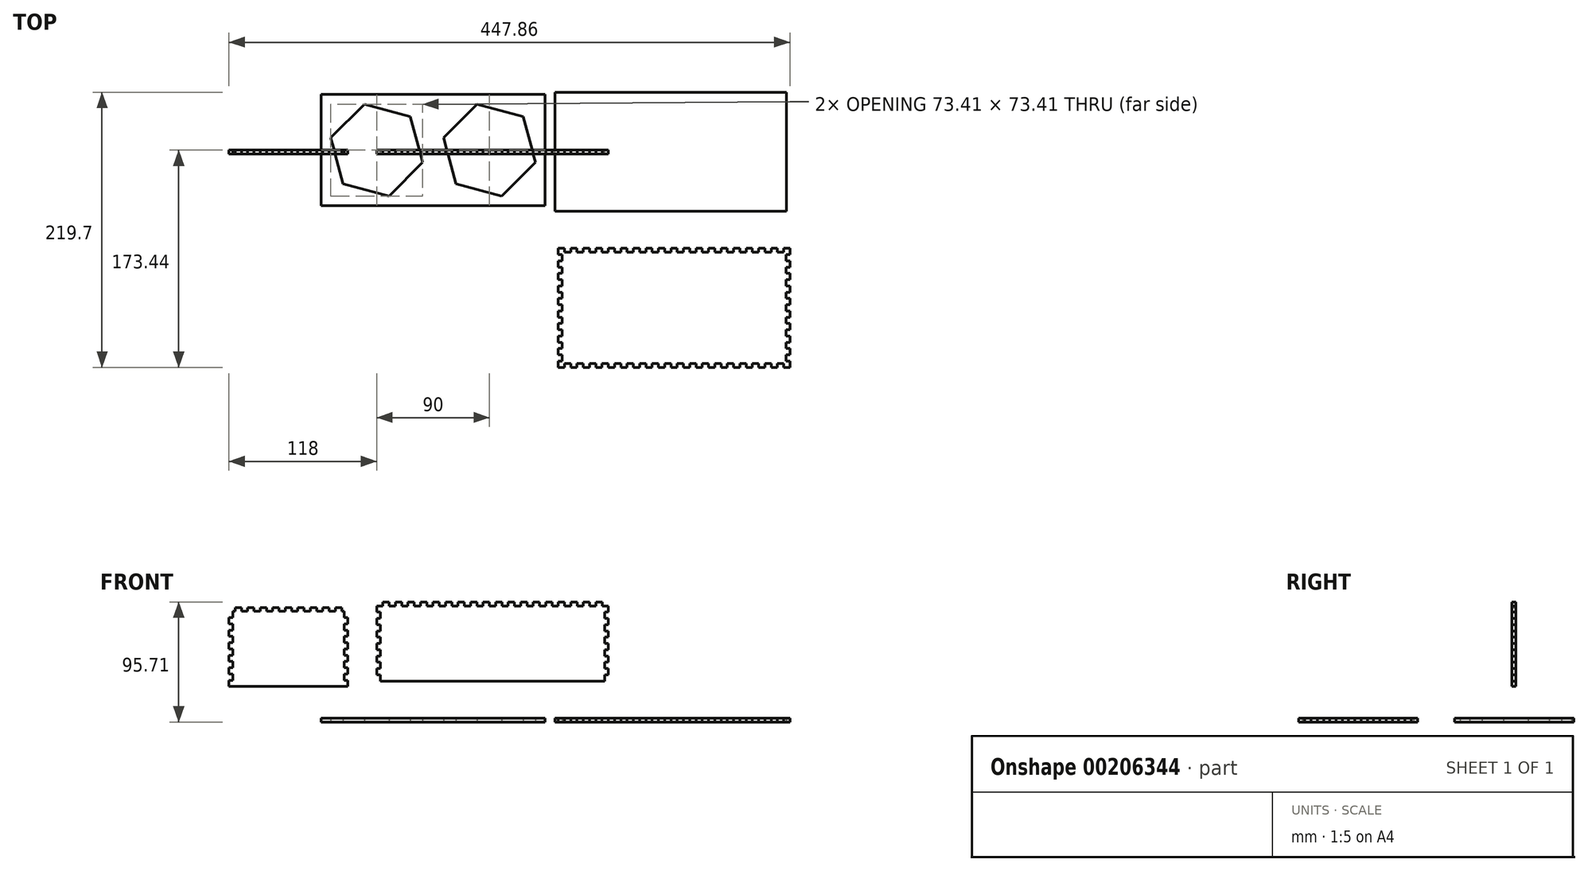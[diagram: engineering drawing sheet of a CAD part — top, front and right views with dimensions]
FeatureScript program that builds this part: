
annotation { "Feature Type Name" : "Feature", "Feature Type Description" : "" }
export const myFeature = defineFeature(function(context is Context, id is Id, definition is map)
    precondition{}
    {
        {
            var Q0;
            Q0=qCreatedBy(makeId("Top.planeOp"),FACE);
            var sketch = newSketch(context, id + "F0", { "sketchPlane" : qUnion([Q0])});
            skLineSegment(sketch, "E0.bottom", {"start": v(-89.5, 44.5) * mm, "end": v(89.5, 44.5) * mm});
            skLineSegment(sketch, "E0.top", {"start": v(-89.5, -44.5) * mm, "end": v(89.5, -44.5) * mm});
            skLineSegment(sketch, "E0.left", {"start": v(-89.5, 44.5) * mm, "end": v(-89.5, -44.5) * mm});
            skLineSegment(sketch, "E0.right", {"start": v(89.5, 44.5) * mm, "end": v(89.5, -44.5) * mm});
            skCircle(sketch, "E1.cCircle", {"center": v(-45, 0) * mm, "radius": 32.9 * mm, "construction": true});
            skLineSegment(sketch, "E1.0", {"start": v(-8.3, -9.84) * mm, "end": v(-35.16, -36.7) * mm});
            skLineSegment(sketch, "E1.1", {"start": v(-35.16, -36.7) * mm, "end": v(-71.87, -26.87) * mm});
            skLineSegment(sketch, "E1.2", {"start": v(-71.87, -26.87) * mm, "end": v(-81.7, 9.84) * mm});
            skLineSegment(sketch, "E1.3", {"start": v(-81.7, 9.84) * mm, "end": v(-54.84, 36.7) * mm});
            skLineSegment(sketch, "E1.4", {"start": v(-54.84, 36.7) * mm, "end": v(-18.13, 26.87) * mm});
            skLineSegment(sketch, "E1.5", {"start": v(-18.13, 26.87) * mm, "end": v(-8.3, -9.84) * mm});
            skPoint(sketch, "E1.0.midPoint", {"position": v(-21.73, -23.27) * mm});
            skCircle(sketch, "E2.cCircle", {"center": v(45, 0) * mm, "radius": 32.9 * mm, "construction": true});
            skLineSegment(sketch, "E2.0", {"start": v(81.7, -9.84) * mm, "end": v(54.84, -36.7) * mm});
            skLineSegment(sketch, "E2.1", {"start": v(54.84, -36.7) * mm, "end": v(18.13, -26.87) * mm});
            skLineSegment(sketch, "E2.2", {"start": v(18.13, -26.87) * mm, "end": v(8.3, 9.84) * mm});
            skLineSegment(sketch, "E2.3", {"start": v(8.3, 9.84) * mm, "end": v(35.16, 36.7) * mm});
            skLineSegment(sketch, "E2.4", {"start": v(35.16, 36.7) * mm, "end": v(71.87, 26.87) * mm});
            skLineSegment(sketch, "E2.5", {"start": v(71.87, 26.87) * mm, "end": v(81.7, -9.84) * mm});
            skPoint(sketch, "E2.0.midPoint", {"position": v(68.27, -23.27) * mm});
            skLineSegment(sketch, "E3", {"start": v(-45, 0) * mm, "end": v(45, 0) * mm, "construction": true});
            skSolve(sketch);
        }
        {
            var Q0;
            Q0 = qSketchRegion(id + "F0", true);
            extrude(context, id + "F1", {"entities" : qUnion([Q0]), "depth" : 3 * mm});
        }
        {
            var Q0;
            Q0=qCreatedBy(makeId("Top.planeOp"),FACE);
            var sketch = newSketch(context, id + "F2", { "sketchPlane" : qUnion([Q0])});
            skLineSegment(sketch, "E4.bottom", {"start": v(97.21, -48.74) * mm, "end": v(282.21, -48.74) * mm});
            skLineSegment(sketch, "E4.top", {"start": v(97.21, 46.26) * mm, "end": v(282.21, 46.26) * mm});
            skLineSegment(sketch, "E4.left", {"start": v(97.21, -48.74) * mm, "end": v(97.21, 46.26) * mm});
            skLineSegment(sketch, "E4.right", {"start": v(282.21, -48.74) * mm, "end": v(282.21, 46.26) * mm});
            skSolve(sketch);
        }
        {
            var Q0;
            Q0 = qSketchRegion(id + "F2", true);
            extrude(context, id + "F3", {"entities" : qUnion([Q0]), "depth" : 3 * mm});
        }
        {
            var Q0;
            Q0=qCreatedBy(makeId("Top.planeOp"),FACE);
            var sketch = newSketch(context, id + "F4", { "sketchPlane" : qUnion([Q0])});
            skLineSegment(sketch, "E5", {"start": v(99.86, -173.44) * mm, "end": v(104.86, -173.44) * mm});
            skLineSegment(sketch, "E6", {"start": v(104.86, -173.44) * mm, "end": v(104.86, -170.44) * mm});
            skLineSegment(sketch, "E7", {"start": v(104.86, -170.44) * mm, "end": v(109.86, -170.44) * mm});
            skLineSegment(sketch, "E8", {"start": v(109.86, -170.44) * mm, "end": v(109.86, -173.44) * mm});
            skLineSegment(sketch, "E9.1.0.0", {"start": v(114.86, -170.44) * mm, "end": v(119.86, -170.44) * mm});
            skLineSegment(sketch, "E9.1.0.1", {"start": v(119.86, -170.44) * mm, "end": v(119.86, -173.44) * mm});
            skLineSegment(sketch, "E9.1.0.2", {"start": v(114.86, -173.44) * mm, "end": v(114.86, -170.44) * mm});
            skLineSegment(sketch, "E9.1.0.3", {"start": v(109.86, -173.44) * mm, "end": v(114.86, -173.44) * mm});
            skLineSegment(sketch, "E9.2.0.0", {"start": v(124.86, -170.44) * mm, "end": v(129.86, -170.44) * mm});
            skLineSegment(sketch, "E9.2.0.1", {"start": v(129.86, -170.44) * mm, "end": v(129.86, -173.44) * mm});
            skLineSegment(sketch, "E9.2.0.2", {"start": v(124.86, -173.44) * mm, "end": v(124.86, -170.44) * mm});
            skLineSegment(sketch, "E9.2.0.3", {"start": v(119.86, -173.44) * mm, "end": v(124.86, -173.44) * mm});
            skLineSegment(sketch, "E9.3.0.0", {"start": v(134.86, -170.44) * mm, "end": v(139.86, -170.44) * mm});
            skLineSegment(sketch, "E9.3.0.1", {"start": v(139.86, -170.44) * mm, "end": v(139.86, -173.44) * mm});
            skLineSegment(sketch, "E9.3.0.2", {"start": v(134.86, -173.44) * mm, "end": v(134.86, -170.44) * mm});
            skLineSegment(sketch, "E9.3.0.3", {"start": v(129.86, -173.44) * mm, "end": v(134.86, -173.44) * mm});
            skLineSegment(sketch, "E9.4.0.0", {"start": v(144.86, -170.44) * mm, "end": v(149.86, -170.44) * mm});
            skLineSegment(sketch, "E9.4.0.1", {"start": v(149.86, -170.44) * mm, "end": v(149.86, -173.44) * mm});
            skLineSegment(sketch, "E9.4.0.2", {"start": v(144.86, -173.44) * mm, "end": v(144.86, -170.44) * mm});
            skLineSegment(sketch, "E9.4.0.3", {"start": v(139.86, -173.44) * mm, "end": v(144.86, -173.44) * mm});
            skLineSegment(sketch, "E9.5.0.0", {"start": v(154.86, -170.44) * mm, "end": v(159.86, -170.44) * mm});
            skLineSegment(sketch, "E9.5.0.1", {"start": v(159.86, -170.44) * mm, "end": v(159.86, -173.44) * mm});
            skLineSegment(sketch, "E9.5.0.2", {"start": v(154.86, -173.44) * mm, "end": v(154.86, -170.44) * mm});
            skLineSegment(sketch, "E9.5.0.3", {"start": v(149.86, -173.44) * mm, "end": v(154.86, -173.44) * mm});
            skLineSegment(sketch, "E9.6.0.0", {"start": v(164.86, -170.44) * mm, "end": v(169.86, -170.44) * mm});
            skLineSegment(sketch, "E9.6.0.1", {"start": v(169.86, -170.44) * mm, "end": v(169.86, -173.44) * mm});
            skLineSegment(sketch, "E9.6.0.2", {"start": v(164.86, -173.44) * mm, "end": v(164.86, -170.44) * mm});
            skLineSegment(sketch, "E9.6.0.3", {"start": v(159.86, -173.44) * mm, "end": v(164.86, -173.44) * mm});
            skLineSegment(sketch, "E9.7.0.0", {"start": v(174.86, -170.44) * mm, "end": v(179.86, -170.44) * mm});
            skLineSegment(sketch, "E9.7.0.1", {"start": v(179.86, -170.44) * mm, "end": v(179.86, -173.44) * mm});
            skLineSegment(sketch, "E9.7.0.2", {"start": v(174.86, -173.44) * mm, "end": v(174.86, -170.44) * mm});
            skLineSegment(sketch, "E9.7.0.3", {"start": v(169.86, -173.44) * mm, "end": v(174.86, -173.44) * mm});
            skLineSegment(sketch, "E9.8.0.0", {"start": v(184.86, -170.44) * mm, "end": v(189.86, -170.44) * mm});
            skLineSegment(sketch, "E9.8.0.1", {"start": v(189.86, -170.44) * mm, "end": v(189.86, -173.44) * mm});
            skLineSegment(sketch, "E9.8.0.2", {"start": v(184.86, -173.44) * mm, "end": v(184.86, -170.44) * mm});
            skLineSegment(sketch, "E9.8.0.3", {"start": v(179.86, -173.44) * mm, "end": v(184.86, -173.44) * mm});
            skLineSegment(sketch, "E9.9.0.0", {"start": v(194.86, -170.44) * mm, "end": v(199.86, -170.44) * mm});
            skLineSegment(sketch, "E9.9.0.1", {"start": v(199.86, -170.44) * mm, "end": v(199.86, -173.44) * mm});
            skLineSegment(sketch, "E9.9.0.2", {"start": v(194.86, -173.44) * mm, "end": v(194.86, -170.44) * mm});
            skLineSegment(sketch, "E9.9.0.3", {"start": v(189.86, -173.44) * mm, "end": v(194.86, -173.44) * mm});
            skLineSegment(sketch, "E9.10.0.0", {"start": v(204.86, -170.44) * mm, "end": v(209.86, -170.44) * mm});
            skLineSegment(sketch, "E9.10.0.1", {"start": v(209.86, -170.44) * mm, "end": v(209.86, -173.44) * mm});
            skLineSegment(sketch, "E9.10.0.2", {"start": v(204.86, -173.44) * mm, "end": v(204.86, -170.44) * mm});
            skLineSegment(sketch, "E9.10.0.3", {"start": v(199.86, -173.44) * mm, "end": v(204.86, -173.44) * mm});
            skLineSegment(sketch, "E9.11.0.0", {"start": v(214.86, -170.44) * mm, "end": v(219.86, -170.44) * mm});
            skLineSegment(sketch, "E9.11.0.1", {"start": v(219.86, -170.44) * mm, "end": v(219.86, -173.44) * mm});
            skLineSegment(sketch, "E9.11.0.2", {"start": v(214.86, -173.44) * mm, "end": v(214.86, -170.44) * mm});
            skLineSegment(sketch, "E9.11.0.3", {"start": v(209.86, -173.44) * mm, "end": v(214.86, -173.44) * mm});
            skLineSegment(sketch, "E9.12.0.0", {"start": v(224.86, -170.44) * mm, "end": v(229.86, -170.44) * mm});
            skLineSegment(sketch, "E9.12.0.1", {"start": v(229.86, -170.44) * mm, "end": v(229.86, -173.44) * mm});
            skLineSegment(sketch, "E9.12.0.2", {"start": v(224.86, -173.44) * mm, "end": v(224.86, -170.44) * mm});
            skLineSegment(sketch, "E9.12.0.3", {"start": v(219.86, -173.44) * mm, "end": v(224.86, -173.44) * mm});
            skLineSegment(sketch, "E9.13.0.0", {"start": v(234.86, -170.44) * mm, "end": v(239.86, -170.44) * mm});
            skLineSegment(sketch, "E9.13.0.1", {"start": v(239.86, -170.44) * mm, "end": v(239.86, -173.44) * mm});
            skLineSegment(sketch, "E9.13.0.2", {"start": v(234.86, -173.44) * mm, "end": v(234.86, -170.44) * mm});
            skLineSegment(sketch, "E9.13.0.3", {"start": v(229.86, -173.44) * mm, "end": v(234.86, -173.44) * mm});
            skLineSegment(sketch, "E9.14.0.0", {"start": v(244.86, -170.44) * mm, "end": v(249.86, -170.44) * mm});
            skLineSegment(sketch, "E9.14.0.1", {"start": v(249.86, -170.44) * mm, "end": v(249.86, -173.44) * mm});
            skLineSegment(sketch, "E9.14.0.2", {"start": v(244.86, -173.44) * mm, "end": v(244.86, -170.44) * mm});
            skLineSegment(sketch, "E9.14.0.3", {"start": v(239.86, -173.44) * mm, "end": v(244.86, -173.44) * mm});
            skLineSegment(sketch, "E9.15.0.0", {"start": v(254.86, -170.44) * mm, "end": v(259.86, -170.44) * mm});
            skLineSegment(sketch, "E9.15.0.1", {"start": v(259.86, -170.44) * mm, "end": v(259.86, -173.44) * mm});
            skLineSegment(sketch, "E9.15.0.2", {"start": v(254.86, -173.44) * mm, "end": v(254.86, -170.44) * mm});
            skLineSegment(sketch, "E9.15.0.3", {"start": v(249.86, -173.44) * mm, "end": v(254.86, -173.44) * mm});
            skLineSegment(sketch, "E9.16.0.0", {"start": v(264.86, -170.44) * mm, "end": v(269.86, -170.44) * mm});
            skLineSegment(sketch, "E9.16.0.1", {"start": v(269.86, -170.44) * mm, "end": v(269.86, -173.44) * mm});
            skLineSegment(sketch, "E9.16.0.2", {"start": v(264.86, -173.44) * mm, "end": v(264.86, -170.44) * mm});
            skLineSegment(sketch, "E9.16.0.3", {"start": v(259.86, -173.44) * mm, "end": v(264.86, -173.44) * mm});
            skLineSegment(sketch, "E9.17.0.0", {"start": v(274.86, -170.44) * mm, "end": v(279.86, -170.44) * mm});
            skLineSegment(sketch, "E9.17.0.1", {"start": v(279.86, -170.44) * mm, "end": v(279.86, -173.44) * mm});
            skLineSegment(sketch, "E9.17.0.2", {"start": v(274.86, -173.44) * mm, "end": v(274.86, -170.44) * mm});
            skLineSegment(sketch, "E9.17.0.3", {"start": v(269.86, -173.44) * mm, "end": v(274.86, -173.44) * mm});
            skLineSegment(sketch, "E9.direction1", {"start": v(99.86, -173.44) * mm, "end": v(109.86, -173.44) * mm, "construction": true});
            skLineSegment(sketch, "E10", {"start": v(279.86, -173.44) * mm, "end": v(284.86, -173.44) * mm});
            skLineSegment(sketch, "E11", {"start": v(99.86, -78.44) * mm, "end": v(104.86, -78.44) * mm});
            skLineSegment(sketch, "E12", {"start": v(104.86, -78.44) * mm, "end": v(104.86, -81.44) * mm});
            skLineSegment(sketch, "E13", {"start": v(104.86, -81.44) * mm, "end": v(109.86, -81.44) * mm});
            skLineSegment(sketch, "E14", {"start": v(109.86, -81.44) * mm, "end": v(109.86, -78.44) * mm});
            skLineSegment(sketch, "E15.1.0.0", {"start": v(109.86, -78.44) * mm, "end": v(114.86, -78.44) * mm});
            skLineSegment(sketch, "E15.1.0.1", {"start": v(114.86, -78.44) * mm, "end": v(114.86, -81.44) * mm});
            skLineSegment(sketch, "E15.1.0.2", {"start": v(119.86, -81.44) * mm, "end": v(119.86, -78.44) * mm});
            skLineSegment(sketch, "E15.1.0.3", {"start": v(114.86, -81.44) * mm, "end": v(119.86, -81.44) * mm});
            skLineSegment(sketch, "E15.2.0.0", {"start": v(119.86, -78.44) * mm, "end": v(124.86, -78.44) * mm});
            skLineSegment(sketch, "E15.2.0.1", {"start": v(124.86, -78.44) * mm, "end": v(124.86, -81.44) * mm});
            skLineSegment(sketch, "E15.2.0.2", {"start": v(129.86, -81.44) * mm, "end": v(129.86, -78.44) * mm});
            skLineSegment(sketch, "E15.2.0.3", {"start": v(124.86, -81.44) * mm, "end": v(129.86, -81.44) * mm});
            skLineSegment(sketch, "E15.3.0.0", {"start": v(129.86, -78.44) * mm, "end": v(134.86, -78.44) * mm});
            skLineSegment(sketch, "E15.3.0.1", {"start": v(134.86, -78.44) * mm, "end": v(134.86, -81.44) * mm});
            skLineSegment(sketch, "E15.3.0.2", {"start": v(139.86, -81.44) * mm, "end": v(139.86, -78.44) * mm});
            skLineSegment(sketch, "E15.3.0.3", {"start": v(134.86, -81.44) * mm, "end": v(139.86, -81.44) * mm});
            skLineSegment(sketch, "E15.4.0.0", {"start": v(139.86, -78.44) * mm, "end": v(144.86, -78.44) * mm});
            skLineSegment(sketch, "E15.4.0.1", {"start": v(144.86, -78.44) * mm, "end": v(144.86, -81.44) * mm});
            skLineSegment(sketch, "E15.4.0.2", {"start": v(149.86, -81.44) * mm, "end": v(149.86, -78.44) * mm});
            skLineSegment(sketch, "E15.4.0.3", {"start": v(144.86, -81.44) * mm, "end": v(149.86, -81.44) * mm});
            skLineSegment(sketch, "E15.5.0.0", {"start": v(149.86, -78.44) * mm, "end": v(154.86, -78.44) * mm});
            skLineSegment(sketch, "E15.5.0.1", {"start": v(154.86, -78.44) * mm, "end": v(154.86, -81.44) * mm});
            skLineSegment(sketch, "E15.5.0.2", {"start": v(159.86, -81.44) * mm, "end": v(159.86, -78.44) * mm});
            skLineSegment(sketch, "E15.5.0.3", {"start": v(154.86, -81.44) * mm, "end": v(159.86, -81.44) * mm});
            skLineSegment(sketch, "E15.6.0.0", {"start": v(159.86, -78.44) * mm, "end": v(164.86, -78.44) * mm});
            skLineSegment(sketch, "E15.6.0.1", {"start": v(164.86, -78.44) * mm, "end": v(164.86, -81.44) * mm});
            skLineSegment(sketch, "E15.6.0.2", {"start": v(169.86, -81.44) * mm, "end": v(169.86, -78.44) * mm});
            skLineSegment(sketch, "E15.6.0.3", {"start": v(164.86, -81.44) * mm, "end": v(169.86, -81.44) * mm});
            skLineSegment(sketch, "E15.7.0.0", {"start": v(169.86, -78.44) * mm, "end": v(174.86, -78.44) * mm});
            skLineSegment(sketch, "E15.7.0.1", {"start": v(174.86, -78.44) * mm, "end": v(174.86, -81.44) * mm});
            skLineSegment(sketch, "E15.7.0.2", {"start": v(179.86, -81.44) * mm, "end": v(179.86, -78.44) * mm});
            skLineSegment(sketch, "E15.7.0.3", {"start": v(174.86, -81.44) * mm, "end": v(179.86, -81.44) * mm});
            skLineSegment(sketch, "E15.8.0.0", {"start": v(179.86, -78.44) * mm, "end": v(184.86, -78.44) * mm});
            skLineSegment(sketch, "E15.8.0.1", {"start": v(184.86, -78.44) * mm, "end": v(184.86, -81.44) * mm});
            skLineSegment(sketch, "E15.8.0.2", {"start": v(189.86, -81.44) * mm, "end": v(189.86, -78.44) * mm});
            skLineSegment(sketch, "E15.8.0.3", {"start": v(184.86, -81.44) * mm, "end": v(189.86, -81.44) * mm});
            skLineSegment(sketch, "E15.9.0.0", {"start": v(189.86, -78.44) * mm, "end": v(194.86, -78.44) * mm});
            skLineSegment(sketch, "E15.9.0.1", {"start": v(194.86, -78.44) * mm, "end": v(194.86, -81.44) * mm});
            skLineSegment(sketch, "E15.9.0.2", {"start": v(199.86, -81.44) * mm, "end": v(199.86, -78.44) * mm});
            skLineSegment(sketch, "E15.9.0.3", {"start": v(194.86, -81.44) * mm, "end": v(199.86, -81.44) * mm});
            skLineSegment(sketch, "E15.10.0.0", {"start": v(199.86, -78.44) * mm, "end": v(204.86, -78.44) * mm});
            skLineSegment(sketch, "E15.10.0.1", {"start": v(204.86, -78.44) * mm, "end": v(204.86, -81.44) * mm});
            skLineSegment(sketch, "E15.10.0.2", {"start": v(209.86, -81.44) * mm, "end": v(209.86, -78.44) * mm});
            skLineSegment(sketch, "E15.10.0.3", {"start": v(204.86, -81.44) * mm, "end": v(209.86, -81.44) * mm});
            skLineSegment(sketch, "E15.11.0.0", {"start": v(209.86, -78.44) * mm, "end": v(214.86, -78.44) * mm});
            skLineSegment(sketch, "E15.11.0.1", {"start": v(214.86, -78.44) * mm, "end": v(214.86, -81.44) * mm});
            skLineSegment(sketch, "E15.11.0.2", {"start": v(219.86, -81.44) * mm, "end": v(219.86, -78.44) * mm});
            skLineSegment(sketch, "E15.11.0.3", {"start": v(214.86, -81.44) * mm, "end": v(219.86, -81.44) * mm});
            skLineSegment(sketch, "E15.12.0.0", {"start": v(219.86, -78.44) * mm, "end": v(224.86, -78.44) * mm});
            skLineSegment(sketch, "E15.12.0.1", {"start": v(224.86, -78.44) * mm, "end": v(224.86, -81.44) * mm});
            skLineSegment(sketch, "E15.12.0.2", {"start": v(229.86, -81.44) * mm, "end": v(229.86, -78.44) * mm});
            skLineSegment(sketch, "E15.12.0.3", {"start": v(224.86, -81.44) * mm, "end": v(229.86, -81.44) * mm});
            skLineSegment(sketch, "E15.13.0.0", {"start": v(229.86, -78.44) * mm, "end": v(234.86, -78.44) * mm});
            skLineSegment(sketch, "E15.13.0.1", {"start": v(234.86, -78.44) * mm, "end": v(234.86, -81.44) * mm});
            skLineSegment(sketch, "E15.13.0.2", {"start": v(239.86, -81.44) * mm, "end": v(239.86, -78.44) * mm});
            skLineSegment(sketch, "E15.13.0.3", {"start": v(234.86, -81.44) * mm, "end": v(239.86, -81.44) * mm});
            skLineSegment(sketch, "E15.14.0.0", {"start": v(239.86, -78.44) * mm, "end": v(244.86, -78.44) * mm});
            skLineSegment(sketch, "E15.14.0.1", {"start": v(244.86, -78.44) * mm, "end": v(244.86, -81.44) * mm});
            skLineSegment(sketch, "E15.14.0.2", {"start": v(249.86, -81.44) * mm, "end": v(249.86, -78.44) * mm});
            skLineSegment(sketch, "E15.14.0.3", {"start": v(244.86, -81.44) * mm, "end": v(249.86, -81.44) * mm});
            skLineSegment(sketch, "E15.15.0.0", {"start": v(249.86, -78.44) * mm, "end": v(254.86, -78.44) * mm});
            skLineSegment(sketch, "E15.15.0.1", {"start": v(254.86, -78.44) * mm, "end": v(254.86, -81.44) * mm});
            skLineSegment(sketch, "E15.15.0.2", {"start": v(259.86, -81.44) * mm, "end": v(259.86, -78.44) * mm});
            skLineSegment(sketch, "E15.15.0.3", {"start": v(254.86, -81.44) * mm, "end": v(259.86, -81.44) * mm});
            skLineSegment(sketch, "E15.16.0.0", {"start": v(259.86, -78.44) * mm, "end": v(264.86, -78.44) * mm});
            skLineSegment(sketch, "E15.16.0.1", {"start": v(264.86, -78.44) * mm, "end": v(264.86, -81.44) * mm});
            skLineSegment(sketch, "E15.16.0.2", {"start": v(269.86, -81.44) * mm, "end": v(269.86, -78.44) * mm});
            skLineSegment(sketch, "E15.16.0.3", {"start": v(264.86, -81.44) * mm, "end": v(269.86, -81.44) * mm});
            skLineSegment(sketch, "E15.17.0.0", {"start": v(269.86, -78.44) * mm, "end": v(274.86, -78.44) * mm});
            skLineSegment(sketch, "E15.17.0.1", {"start": v(274.86, -78.44) * mm, "end": v(274.86, -81.44) * mm});
            skLineSegment(sketch, "E15.17.0.2", {"start": v(279.86, -81.44) * mm, "end": v(279.86, -78.44) * mm});
            skLineSegment(sketch, "E15.17.0.3", {"start": v(274.86, -81.44) * mm, "end": v(279.86, -81.44) * mm});
            skLineSegment(sketch, "E15.direction1", {"start": v(99.86, -78.44) * mm, "end": v(109.86, -78.44) * mm, "construction": true});
            skLineSegment(sketch, "E16", {"start": v(279.86, -78.44) * mm, "end": v(284.86, -78.44) * mm});
            skLineSegment(sketch, "E17", {"start": v(99.86, -78.44) * mm, "end": v(99.86, -83.44) * mm});
            skLineSegment(sketch, "E18", {"start": v(99.86, -83.44) * mm, "end": v(102.86, -83.44) * mm});
            skLineSegment(sketch, "E19", {"start": v(102.86, -83.44) * mm, "end": v(102.86, -88.44) * mm});
            skLineSegment(sketch, "E20", {"start": v(102.86, -88.44) * mm, "end": v(99.86, -88.44) * mm});
            skLineSegment(sketch, "E21.0.1.0", {"start": v(99.86, -88.44) * mm, "end": v(99.86, -93.44) * mm});
            skLineSegment(sketch, "E21.0.1.1", {"start": v(102.86, -98.44) * mm, "end": v(99.86, -98.44) * mm});
            skLineSegment(sketch, "E21.0.1.2", {"start": v(102.86, -93.44) * mm, "end": v(102.86, -98.44) * mm});
            skLineSegment(sketch, "E21.0.1.3", {"start": v(99.86, -93.44) * mm, "end": v(102.86, -93.44) * mm});
            skLineSegment(sketch, "E21.0.2.0", {"start": v(99.86, -98.44) * mm, "end": v(99.86, -103.44) * mm});
            skLineSegment(sketch, "E21.0.2.1", {"start": v(102.86, -108.44) * mm, "end": v(99.86, -108.44) * mm});
            skLineSegment(sketch, "E21.0.2.2", {"start": v(102.86, -103.44) * mm, "end": v(102.86, -108.44) * mm});
            skLineSegment(sketch, "E21.0.2.3", {"start": v(99.86, -103.44) * mm, "end": v(102.86, -103.44) * mm});
            skLineSegment(sketch, "E21.0.3.0", {"start": v(99.86, -108.44) * mm, "end": v(99.86, -113.44) * mm});
            skLineSegment(sketch, "E21.0.3.1", {"start": v(102.86, -118.44) * mm, "end": v(99.86, -118.44) * mm});
            skLineSegment(sketch, "E21.0.3.2", {"start": v(102.86, -113.44) * mm, "end": v(102.86, -118.44) * mm});
            skLineSegment(sketch, "E21.0.3.3", {"start": v(99.86, -113.44) * mm, "end": v(102.86, -113.44) * mm});
            skLineSegment(sketch, "E21.0.4.0", {"start": v(99.86, -118.44) * mm, "end": v(99.86, -123.44) * mm});
            skLineSegment(sketch, "E21.0.4.1", {"start": v(102.86, -128.44) * mm, "end": v(99.86, -128.44) * mm});
            skLineSegment(sketch, "E21.0.4.2", {"start": v(102.86, -123.44) * mm, "end": v(102.86, -128.44) * mm});
            skLineSegment(sketch, "E21.0.4.3", {"start": v(99.86, -123.44) * mm, "end": v(102.86, -123.44) * mm});
            skLineSegment(sketch, "E21.0.5.0", {"start": v(99.86, -128.44) * mm, "end": v(99.86, -133.44) * mm});
            skLineSegment(sketch, "E21.0.5.1", {"start": v(102.86, -138.44) * mm, "end": v(99.86, -138.44) * mm});
            skLineSegment(sketch, "E21.0.5.2", {"start": v(102.86, -133.44) * mm, "end": v(102.86, -138.44) * mm});
            skLineSegment(sketch, "E21.0.5.3", {"start": v(99.86, -133.44) * mm, "end": v(102.86, -133.44) * mm});
            skLineSegment(sketch, "E21.0.6.0", {"start": v(99.86, -138.44) * mm, "end": v(99.86, -143.44) * mm});
            skLineSegment(sketch, "E21.0.6.1", {"start": v(102.86, -148.44) * mm, "end": v(99.86, -148.44) * mm});
            skLineSegment(sketch, "E21.0.6.2", {"start": v(102.86, -143.44) * mm, "end": v(102.86, -148.44) * mm});
            skLineSegment(sketch, "E21.0.6.3", {"start": v(99.86, -143.44) * mm, "end": v(102.86, -143.44) * mm});
            skLineSegment(sketch, "E21.0.7.0", {"start": v(99.86, -148.44) * mm, "end": v(99.86, -153.44) * mm});
            skLineSegment(sketch, "E21.0.7.1", {"start": v(102.86, -158.44) * mm, "end": v(99.86, -158.44) * mm});
            skLineSegment(sketch, "E21.0.7.2", {"start": v(102.86, -153.44) * mm, "end": v(102.86, -158.44) * mm});
            skLineSegment(sketch, "E21.0.7.3", {"start": v(99.86, -153.44) * mm, "end": v(102.86, -153.44) * mm});
            skLineSegment(sketch, "E21.0.8.0", {"start": v(99.86, -158.44) * mm, "end": v(99.86, -163.44) * mm});
            skLineSegment(sketch, "E21.0.8.1", {"start": v(102.86, -168.44) * mm, "end": v(99.86, -168.44) * mm});
            skLineSegment(sketch, "E21.0.8.2", {"start": v(102.86, -163.44) * mm, "end": v(102.86, -168.44) * mm});
            skLineSegment(sketch, "E21.0.8.3", {"start": v(99.86, -163.44) * mm, "end": v(102.86, -163.44) * mm});
            skLineSegment(sketch, "E21.direction1", {"start": v(99.86, -88.44) * mm, "end": v(124.86, -88.44) * mm, "construction": true});
            skLineSegment(sketch, "E21.direction2", {"start": v(99.86, -88.44) * mm, "end": v(99.86, -98.44) * mm, "construction": true});
            skLineSegment(sketch, "E22", {"start": v(99.86, -168.44) * mm, "end": v(99.86, -173.44) * mm});
            skLineSegment(sketch, "E23", {"start": v(284.86, -78.44) * mm, "end": v(284.86, -83.44) * mm});
            skLineSegment(sketch, "E24", {"start": v(284.86, -83.44) * mm, "end": v(281.86, -83.44) * mm});
            skLineSegment(sketch, "E25", {"start": v(281.86, -83.44) * mm, "end": v(281.86, -88.44) * mm});
            skLineSegment(sketch, "E26", {"start": v(281.86, -88.44) * mm, "end": v(284.86, -88.44) * mm});
            skLineSegment(sketch, "E27.0.1.0", {"start": v(281.86, -93.44) * mm, "end": v(281.86, -98.44) * mm});
            skLineSegment(sketch, "E27.0.1.1", {"start": v(284.86, -88.44) * mm, "end": v(284.86, -93.44) * mm});
            skLineSegment(sketch, "E27.0.1.2", {"start": v(284.86, -93.44) * mm, "end": v(281.86, -93.44) * mm});
            skLineSegment(sketch, "E27.0.1.3", {"start": v(281.86, -98.44) * mm, "end": v(284.86, -98.44) * mm});
            skLineSegment(sketch, "E27.0.2.0", {"start": v(281.86, -103.44) * mm, "end": v(281.86, -108.44) * mm});
            skLineSegment(sketch, "E27.0.2.1", {"start": v(284.86, -98.44) * mm, "end": v(284.86, -103.44) * mm});
            skLineSegment(sketch, "E27.0.2.2", {"start": v(284.86, -103.44) * mm, "end": v(281.86, -103.44) * mm});
            skLineSegment(sketch, "E27.0.2.3", {"start": v(281.86, -108.44) * mm, "end": v(284.86, -108.44) * mm});
            skLineSegment(sketch, "E27.0.3.0", {"start": v(281.86, -113.44) * mm, "end": v(281.86, -118.44) * mm});
            skLineSegment(sketch, "E27.0.3.1", {"start": v(284.86, -108.44) * mm, "end": v(284.86, -113.44) * mm});
            skLineSegment(sketch, "E27.0.3.2", {"start": v(284.86, -113.44) * mm, "end": v(281.86, -113.44) * mm});
            skLineSegment(sketch, "E27.0.3.3", {"start": v(281.86, -118.44) * mm, "end": v(284.86, -118.44) * mm});
            skLineSegment(sketch, "E27.0.4.0", {"start": v(281.86, -123.44) * mm, "end": v(281.86, -128.44) * mm});
            skLineSegment(sketch, "E27.0.4.1", {"start": v(284.86, -118.44) * mm, "end": v(284.86, -123.44) * mm});
            skLineSegment(sketch, "E27.0.4.2", {"start": v(284.86, -123.44) * mm, "end": v(281.86, -123.44) * mm});
            skLineSegment(sketch, "E27.0.4.3", {"start": v(281.86, -128.44) * mm, "end": v(284.86, -128.44) * mm});
            skLineSegment(sketch, "E27.0.5.0", {"start": v(281.86, -133.44) * mm, "end": v(281.86, -138.44) * mm});
            skLineSegment(sketch, "E27.0.5.1", {"start": v(284.86, -128.44) * mm, "end": v(284.86, -133.44) * mm});
            skLineSegment(sketch, "E27.0.5.2", {"start": v(284.86, -133.44) * mm, "end": v(281.86, -133.44) * mm});
            skLineSegment(sketch, "E27.0.5.3", {"start": v(281.86, -138.44) * mm, "end": v(284.86, -138.44) * mm});
            skLineSegment(sketch, "E27.0.6.0", {"start": v(281.86, -143.44) * mm, "end": v(281.86, -148.44) * mm});
            skLineSegment(sketch, "E27.0.6.1", {"start": v(284.86, -138.44) * mm, "end": v(284.86, -143.44) * mm});
            skLineSegment(sketch, "E27.0.6.2", {"start": v(284.86, -143.44) * mm, "end": v(281.86, -143.44) * mm});
            skLineSegment(sketch, "E27.0.6.3", {"start": v(281.86, -148.44) * mm, "end": v(284.86, -148.44) * mm});
            skLineSegment(sketch, "E27.0.7.0", {"start": v(281.86, -153.44) * mm, "end": v(281.86, -158.44) * mm});
            skLineSegment(sketch, "E27.0.7.1", {"start": v(284.86, -148.44) * mm, "end": v(284.86, -153.44) * mm});
            skLineSegment(sketch, "E27.0.7.2", {"start": v(284.86, -153.44) * mm, "end": v(281.86, -153.44) * mm});
            skLineSegment(sketch, "E27.0.7.3", {"start": v(281.86, -158.44) * mm, "end": v(284.86, -158.44) * mm});
            skLineSegment(sketch, "E27.0.8.0", {"start": v(281.86, -163.44) * mm, "end": v(281.86, -168.44) * mm});
            skLineSegment(sketch, "E27.0.8.1", {"start": v(284.86, -158.44) * mm, "end": v(284.86, -163.44) * mm});
            skLineSegment(sketch, "E27.0.8.2", {"start": v(284.86, -163.44) * mm, "end": v(281.86, -163.44) * mm});
            skLineSegment(sketch, "E27.0.8.3", {"start": v(281.86, -168.44) * mm, "end": v(284.86, -168.44) * mm});
            skLineSegment(sketch, "E27.direction1", {"start": v(281.86, -88.44) * mm, "end": v(306.86, -88.44) * mm, "construction": true});
            skLineSegment(sketch, "E27.direction2", {"start": v(281.86, -88.44) * mm, "end": v(281.86, -98.44) * mm, "construction": true});
            skLineSegment(sketch, "E28", {"start": v(284.86, -168.44) * mm, "end": v(284.86, -173.44) * mm});
            skSolve(sketch);
        }
        {
            var Q0;
            Q0 = qSketchRegion(id + "F4", true);
            extrude(context, id + "F5", {"entities" : qUnion([Q0]), "depth" : 3 * mm});
        }
        {
            var Q0;
            Q0=qCreatedBy(makeId("Front.planeOp"),FACE);
            var sketch = newSketch(context, id + "F6", { "sketchPlane" : qUnion([Q0])});
            skLineSegment(sketch, "E29", {"start": v(-45.05, 92.7) * mm, "end": v(-40.05, 92.7) * mm});
            skLineSegment(sketch, "E30", {"start": v(-40.05, 92.7) * mm, "end": v(-40.05, 95.7) * mm});
            skLineSegment(sketch, "E31", {"start": v(-40.05, 95.7) * mm, "end": v(-35.05, 95.7) * mm});
            skLineSegment(sketch, "E32", {"start": v(-35.05, 95.7) * mm, "end": v(-35.05, 92.7) * mm});
            skLineSegment(sketch, "E33.1.0.0", {"start": v(-30.05, 95.7) * mm, "end": v(-25.05, 95.7) * mm});
            skLineSegment(sketch, "E33.1.0.1", {"start": v(-30.05, 92.7) * mm, "end": v(-30.05, 95.7) * mm});
            skLineSegment(sketch, "E33.1.0.2", {"start": v(-35.05, 92.7) * mm, "end": v(-30.05, 92.7) * mm});
            skLineSegment(sketch, "E33.1.0.3", {"start": v(-25.05, 95.7) * mm, "end": v(-25.05, 92.7) * mm});
            skLineSegment(sketch, "E33.2.0.0", {"start": v(-20.05, 95.7) * mm, "end": v(-15.05, 95.7) * mm});
            skLineSegment(sketch, "E33.2.0.1", {"start": v(-20.05, 92.7) * mm, "end": v(-20.05, 95.7) * mm});
            skLineSegment(sketch, "E33.2.0.2", {"start": v(-25.05, 92.7) * mm, "end": v(-20.05, 92.7) * mm});
            skLineSegment(sketch, "E33.2.0.3", {"start": v(-15.05, 95.7) * mm, "end": v(-15.05, 92.7) * mm});
            skLineSegment(sketch, "E33.3.0.0", {"start": v(-10.05, 95.7) * mm, "end": v(-5.05, 95.7) * mm});
            skLineSegment(sketch, "E33.3.0.1", {"start": v(-10.05, 92.7) * mm, "end": v(-10.05, 95.7) * mm});
            skLineSegment(sketch, "E33.3.0.2", {"start": v(-15.05, 92.7) * mm, "end": v(-10.05, 92.7) * mm});
            skLineSegment(sketch, "E33.3.0.3", {"start": v(-5.05, 95.7) * mm, "end": v(-5.05, 92.7) * mm});
            skLineSegment(sketch, "E33.4.0.0", {"start": v(-0.05, 95.7) * mm, "end": v(4.95, 95.7) * mm});
            skLineSegment(sketch, "E33.4.0.1", {"start": v(-0.05, 92.7) * mm, "end": v(-0.05, 95.7) * mm});
            skLineSegment(sketch, "E33.4.0.2", {"start": v(-5.05, 92.7) * mm, "end": v(-0.05, 92.7) * mm});
            skLineSegment(sketch, "E33.4.0.3", {"start": v(4.95, 95.7) * mm, "end": v(4.95, 92.7) * mm});
            skLineSegment(sketch, "E33.5.0.0", {"start": v(9.95, 95.7) * mm, "end": v(14.95, 95.7) * mm});
            skLineSegment(sketch, "E33.5.0.1", {"start": v(9.95, 92.7) * mm, "end": v(9.95, 95.7) * mm});
            skLineSegment(sketch, "E33.5.0.2", {"start": v(4.95, 92.7) * mm, "end": v(9.95, 92.7) * mm});
            skLineSegment(sketch, "E33.5.0.3", {"start": v(14.95, 95.7) * mm, "end": v(14.95, 92.7) * mm});
            skLineSegment(sketch, "E33.6.0.0", {"start": v(19.95, 95.7) * mm, "end": v(24.95, 95.7) * mm});
            skLineSegment(sketch, "E33.6.0.1", {"start": v(19.95, 92.7) * mm, "end": v(19.95, 95.7) * mm});
            skLineSegment(sketch, "E33.6.0.2", {"start": v(14.95, 92.7) * mm, "end": v(19.95, 92.7) * mm});
            skLineSegment(sketch, "E33.6.0.3", {"start": v(24.95, 95.7) * mm, "end": v(24.95, 92.7) * mm});
            skLineSegment(sketch, "E33.7.0.0", {"start": v(29.95, 95.7) * mm, "end": v(34.95, 95.7) * mm});
            skLineSegment(sketch, "E33.7.0.1", {"start": v(29.95, 92.7) * mm, "end": v(29.95, 95.7) * mm});
            skLineSegment(sketch, "E33.7.0.2", {"start": v(24.95, 92.7) * mm, "end": v(29.95, 92.7) * mm});
            skLineSegment(sketch, "E33.7.0.3", {"start": v(34.95, 95.7) * mm, "end": v(34.95, 92.7) * mm});
            skLineSegment(sketch, "E33.8.0.0", {"start": v(39.95, 95.7) * mm, "end": v(44.95, 95.7) * mm});
            skLineSegment(sketch, "E33.8.0.1", {"start": v(39.95, 92.7) * mm, "end": v(39.95, 95.7) * mm});
            skLineSegment(sketch, "E33.8.0.2", {"start": v(34.95, 92.7) * mm, "end": v(39.95, 92.7) * mm});
            skLineSegment(sketch, "E33.8.0.3", {"start": v(44.95, 95.7) * mm, "end": v(44.95, 92.7) * mm});
            skLineSegment(sketch, "E33.9.0.0", {"start": v(49.95, 95.7) * mm, "end": v(54.95, 95.7) * mm});
            skLineSegment(sketch, "E33.9.0.1", {"start": v(49.95, 92.7) * mm, "end": v(49.95, 95.7) * mm});
            skLineSegment(sketch, "E33.9.0.2", {"start": v(44.95, 92.7) * mm, "end": v(49.95, 92.7) * mm});
            skLineSegment(sketch, "E33.9.0.3", {"start": v(54.95, 95.7) * mm, "end": v(54.95, 92.7) * mm});
            skLineSegment(sketch, "E33.10.0.0", {"start": v(59.95, 95.7) * mm, "end": v(64.95, 95.7) * mm});
            skLineSegment(sketch, "E33.10.0.1", {"start": v(59.95, 92.7) * mm, "end": v(59.95, 95.7) * mm});
            skLineSegment(sketch, "E33.10.0.2", {"start": v(54.95, 92.7) * mm, "end": v(59.95, 92.7) * mm});
            skLineSegment(sketch, "E33.10.0.3", {"start": v(64.95, 95.7) * mm, "end": v(64.95, 92.7) * mm});
            skLineSegment(sketch, "E33.11.0.0", {"start": v(69.95, 95.7) * mm, "end": v(74.95, 95.7) * mm});
            skLineSegment(sketch, "E33.11.0.1", {"start": v(69.95, 92.7) * mm, "end": v(69.95, 95.7) * mm});
            skLineSegment(sketch, "E33.11.0.2", {"start": v(64.95, 92.7) * mm, "end": v(69.95, 92.7) * mm});
            skLineSegment(sketch, "E33.11.0.3", {"start": v(74.95, 95.7) * mm, "end": v(74.95, 92.7) * mm});
            skLineSegment(sketch, "E33.12.0.0", {"start": v(79.95, 95.7) * mm, "end": v(84.95, 95.7) * mm});
            skLineSegment(sketch, "E33.12.0.1", {"start": v(79.95, 92.7) * mm, "end": v(79.95, 95.7) * mm});
            skLineSegment(sketch, "E33.12.0.2", {"start": v(74.95, 92.7) * mm, "end": v(79.95, 92.7) * mm});
            skLineSegment(sketch, "E33.12.0.3", {"start": v(84.95, 95.7) * mm, "end": v(84.95, 92.7) * mm});
            skLineSegment(sketch, "E33.13.0.0", {"start": v(89.95, 95.7) * mm, "end": v(94.95, 95.7) * mm});
            skLineSegment(sketch, "E33.13.0.1", {"start": v(89.95, 92.7) * mm, "end": v(89.95, 95.7) * mm});
            skLineSegment(sketch, "E33.13.0.2", {"start": v(84.95, 92.7) * mm, "end": v(89.95, 92.7) * mm});
            skLineSegment(sketch, "E33.13.0.3", {"start": v(94.95, 95.7) * mm, "end": v(94.95, 92.7) * mm});
            skLineSegment(sketch, "E33.14.0.0", {"start": v(99.95, 95.7) * mm, "end": v(104.95, 95.7) * mm});
            skLineSegment(sketch, "E33.14.0.1", {"start": v(99.95, 92.7) * mm, "end": v(99.95, 95.7) * mm});
            skLineSegment(sketch, "E33.14.0.2", {"start": v(94.95, 92.7) * mm, "end": v(99.95, 92.7) * mm});
            skLineSegment(sketch, "E33.14.0.3", {"start": v(104.95, 95.7) * mm, "end": v(104.95, 92.7) * mm});
            skLineSegment(sketch, "E33.15.0.0", {"start": v(109.95, 95.7) * mm, "end": v(114.95, 95.7) * mm});
            skLineSegment(sketch, "E33.15.0.1", {"start": v(109.95, 92.7) * mm, "end": v(109.95, 95.7) * mm});
            skLineSegment(sketch, "E33.15.0.2", {"start": v(104.95, 92.7) * mm, "end": v(109.95, 92.7) * mm});
            skLineSegment(sketch, "E33.15.0.3", {"start": v(114.95, 95.7) * mm, "end": v(114.95, 92.7) * mm});
            skLineSegment(sketch, "E33.16.0.0", {"start": v(119.95, 95.7) * mm, "end": v(124.95, 95.7) * mm});
            skLineSegment(sketch, "E33.16.0.1", {"start": v(119.95, 92.7) * mm, "end": v(119.95, 95.7) * mm});
            skLineSegment(sketch, "E33.16.0.2", {"start": v(114.95, 92.7) * mm, "end": v(119.95, 92.7) * mm});
            skLineSegment(sketch, "E33.16.0.3", {"start": v(124.95, 95.7) * mm, "end": v(124.95, 92.7) * mm});
            skLineSegment(sketch, "E33.17.0.0", {"start": v(129.95, 95.7) * mm, "end": v(134.95, 95.7) * mm});
            skLineSegment(sketch, "E33.17.0.1", {"start": v(129.95, 92.7) * mm, "end": v(129.95, 95.7) * mm});
            skLineSegment(sketch, "E33.17.0.2", {"start": v(124.95, 92.7) * mm, "end": v(129.95, 92.7) * mm});
            skLineSegment(sketch, "E33.17.0.3", {"start": v(134.95, 95.7) * mm, "end": v(134.95, 92.7) * mm});
            skLineSegment(sketch, "E33.direction1", {"start": v(-45.05, 92.7) * mm, "end": v(-35.05, 92.7) * mm, "construction": true});
            skLineSegment(sketch, "E34", {"start": v(139.95, 92.7) * mm, "end": v(134.95, 92.7) * mm});
            skLineSegment(sketch, "E35", {"start": v(-45.05, 92.7) * mm, "end": v(-45.05, 87.7) * mm});
            skLineSegment(sketch, "E36", {"start": v(-45.05, 87.7) * mm, "end": v(-42.05, 87.7) * mm});
            skLineSegment(sketch, "E37", {"start": v(-42.05, 87.7) * mm, "end": v(-42.05, 82.7) * mm});
            skLineSegment(sketch, "E38", {"start": v(-42.05, 82.7) * mm, "end": v(-45.05, 82.7) * mm});
            skLineSegment(sketch, "E39.0.1.0", {"start": v(-45.05, 77.7) * mm, "end": v(-42.05, 77.7) * mm});
            skLineSegment(sketch, "E39.0.1.1", {"start": v(-42.05, 72.7) * mm, "end": v(-45.05, 72.7) * mm});
            skLineSegment(sketch, "E39.0.1.2", {"start": v(-42.05, 77.7) * mm, "end": v(-42.05, 72.7) * mm});
            skLineSegment(sketch, "E39.0.1.3", {"start": v(-45.05, 82.7) * mm, "end": v(-45.05, 77.7) * mm});
            skLineSegment(sketch, "E39.0.2.0", {"start": v(-45.05, 67.7) * mm, "end": v(-42.05, 67.7) * mm});
            skLineSegment(sketch, "E39.0.2.1", {"start": v(-42.05, 62.7) * mm, "end": v(-45.05, 62.7) * mm});
            skLineSegment(sketch, "E39.0.2.2", {"start": v(-42.05, 67.7) * mm, "end": v(-42.05, 62.7) * mm});
            skLineSegment(sketch, "E39.0.2.3", {"start": v(-45.05, 72.7) * mm, "end": v(-45.05, 67.7) * mm});
            skLineSegment(sketch, "E39.0.3.0", {"start": v(-45.05, 57.7) * mm, "end": v(-42.05, 57.7) * mm});
            skLineSegment(sketch, "E39.0.3.1", {"start": v(-42.05, 52.7) * mm, "end": v(-45.05, 52.7) * mm});
            skLineSegment(sketch, "E39.0.3.2", {"start": v(-42.05, 57.7) * mm, "end": v(-42.05, 52.7) * mm});
            skLineSegment(sketch, "E39.0.3.3", {"start": v(-45.05, 62.7) * mm, "end": v(-45.05, 57.7) * mm});
            skLineSegment(sketch, "E39.0.4.0", {"start": v(-45.05, 47.7) * mm, "end": v(-42.05, 47.7) * mm});
            skLineSegment(sketch, "E39.0.4.1", {"start": v(-42.05, 42.7) * mm, "end": v(-45.05, 42.7) * mm});
            skLineSegment(sketch, "E39.0.4.2", {"start": v(-42.05, 47.7) * mm, "end": v(-42.05, 42.7) * mm});
            skLineSegment(sketch, "E39.0.4.3", {"start": v(-45.05, 52.7) * mm, "end": v(-45.05, 47.7) * mm});
            skLineSegment(sketch, "E39.0.5.0", {"start": v(-45.05, 37.7) * mm, "end": v(-42.05, 37.7) * mm});
            skLineSegment(sketch, "E39.0.5.2", {"start": v(-42.05, 37.7) * mm, "end": v(-42.05, 32.7) * mm});
            skLineSegment(sketch, "E39.0.5.3", {"start": v(-45.05, 42.7) * mm, "end": v(-45.05, 37.7) * mm});
            skLineSegment(sketch, "E39.direction1", {"start": v(-45.05, 82.7) * mm, "end": v(-20.05, 82.7) * mm, "construction": true});
            skLineSegment(sketch, "E39.direction2", {"start": v(-45.05, 82.7) * mm, "end": v(-45.05, 72.7) * mm, "construction": true});
            skLineSegment(sketch, "E40", {"start": v(-42.05, 32.7) * mm, "end": v(136.95, 32.7) * mm});
            skLineSegment(sketch, "E41", {"start": v(139.95, 92.7) * mm, "end": v(139.95, 87.7) * mm});
            skLineSegment(sketch, "E42", {"start": v(139.95, 87.7) * mm, "end": v(136.95, 87.7) * mm});
            skLineSegment(sketch, "E43", {"start": v(136.95, 87.7) * mm, "end": v(136.95, 82.7) * mm});
            skLineSegment(sketch, "E44", {"start": v(136.95, 82.7) * mm, "end": v(139.95, 82.7) * mm});
            skLineSegment(sketch, "E45.0.1.0", {"start": v(139.95, 82.7) * mm, "end": v(139.95, 77.7) * mm});
            skLineSegment(sketch, "E45.0.1.1", {"start": v(136.95, 77.7) * mm, "end": v(136.95, 72.7) * mm});
            skLineSegment(sketch, "E45.0.1.2", {"start": v(139.95, 77.7) * mm, "end": v(136.95, 77.7) * mm});
            skLineSegment(sketch, "E45.0.1.3", {"start": v(136.95, 72.7) * mm, "end": v(139.95, 72.7) * mm});
            skLineSegment(sketch, "E45.0.2.0", {"start": v(139.95, 72.7) * mm, "end": v(139.95, 67.7) * mm});
            skLineSegment(sketch, "E45.0.2.1", {"start": v(136.95, 67.7) * mm, "end": v(136.95, 62.7) * mm});
            skLineSegment(sketch, "E45.0.2.2", {"start": v(139.95, 67.7) * mm, "end": v(136.95, 67.7) * mm});
            skLineSegment(sketch, "E45.0.2.3", {"start": v(136.95, 62.7) * mm, "end": v(139.95, 62.7) * mm});
            skLineSegment(sketch, "E45.0.3.0", {"start": v(139.95, 62.7) * mm, "end": v(139.95, 57.7) * mm});
            skLineSegment(sketch, "E45.0.3.1", {"start": v(136.95, 57.7) * mm, "end": v(136.95, 52.7) * mm});
            skLineSegment(sketch, "E45.0.3.2", {"start": v(139.95, 57.7) * mm, "end": v(136.95, 57.7) * mm});
            skLineSegment(sketch, "E45.0.3.3", {"start": v(136.95, 52.7) * mm, "end": v(139.95, 52.7) * mm});
            skLineSegment(sketch, "E45.0.4.0", {"start": v(139.95, 52.7) * mm, "end": v(139.95, 47.7) * mm});
            skLineSegment(sketch, "E45.0.4.1", {"start": v(136.95, 47.7) * mm, "end": v(136.95, 42.7) * mm});
            skLineSegment(sketch, "E45.0.4.2", {"start": v(139.95, 47.7) * mm, "end": v(136.95, 47.7) * mm});
            skLineSegment(sketch, "E45.0.4.3", {"start": v(136.95, 42.7) * mm, "end": v(139.95, 42.7) * mm});
            skLineSegment(sketch, "E45.0.5.0", {"start": v(139.95, 42.7) * mm, "end": v(139.95, 37.7) * mm});
            skLineSegment(sketch, "E45.0.5.1", {"start": v(136.95, 37.7) * mm, "end": v(136.95, 32.7) * mm});
            skLineSegment(sketch, "E45.0.5.2", {"start": v(139.95, 37.7) * mm, "end": v(136.95, 37.7) * mm});
            skLineSegment(sketch, "E45.direction1", {"start": v(136.95, 82.7) * mm, "end": v(161.95, 82.7) * mm, "construction": true});
            skLineSegment(sketch, "E45.direction2", {"start": v(136.95, 82.7) * mm, "end": v(136.95, 72.7) * mm, "construction": true});
            skSolve(sketch);
        }
        {
            var Q0;
            Q0 = qSketchRegion(id + "F6", true);
            extrude(context, id + "F7", {"entities" : qUnion([Q0]), "depth" : 3 * mm});
        }
        {
            var Q0;
            Q0=qCreatedBy(makeId("Front.planeOp"),FACE);
            var sketch = newSketch(context, id + "F8", { "sketchPlane" : qUnion([Q0])});
            skLineSegment(sketch, "E46", {"start": v(-158, 88.32) * mm, "end": v(-158, 91.32) * mm});
            skLineSegment(sketch, "E47", {"start": v(-158, 91.32) * mm, "end": v(-153, 91.32) * mm});
            skLineSegment(sketch, "E48", {"start": v(-153, 91.32) * mm, "end": v(-153, 88.32) * mm});
            skLineSegment(sketch, "E49.1.0.0", {"start": v(-153, 88.32) * mm, "end": v(-148, 88.32) * mm});
            skLineSegment(sketch, "E49.1.0.1", {"start": v(-143, 91.32) * mm, "end": v(-143, 88.32) * mm});
            skLineSegment(sketch, "E49.1.0.2", {"start": v(-148, 88.32) * mm, "end": v(-148, 91.32) * mm});
            skLineSegment(sketch, "E49.1.0.3", {"start": v(-148, 91.32) * mm, "end": v(-143, 91.32) * mm});
            skLineSegment(sketch, "E49.2.0.0", {"start": v(-143, 88.32) * mm, "end": v(-138, 88.32) * mm});
            skLineSegment(sketch, "E49.2.0.1", {"start": v(-133, 91.32) * mm, "end": v(-133, 88.32) * mm});
            skLineSegment(sketch, "E49.2.0.2", {"start": v(-138, 88.32) * mm, "end": v(-138, 91.32) * mm});
            skLineSegment(sketch, "E49.2.0.3", {"start": v(-138, 91.32) * mm, "end": v(-133, 91.32) * mm});
            skLineSegment(sketch, "E49.3.0.0", {"start": v(-133, 88.32) * mm, "end": v(-128, 88.32) * mm});
            skLineSegment(sketch, "E49.3.0.1", {"start": v(-123, 91.32) * mm, "end": v(-123, 88.32) * mm});
            skLineSegment(sketch, "E49.3.0.2", {"start": v(-128, 88.32) * mm, "end": v(-128, 91.32) * mm});
            skLineSegment(sketch, "E49.3.0.3", {"start": v(-128, 91.32) * mm, "end": v(-123, 91.32) * mm});
            skLineSegment(sketch, "E49.4.0.0", {"start": v(-123, 88.32) * mm, "end": v(-118, 88.32) * mm});
            skLineSegment(sketch, "E49.4.0.1", {"start": v(-113, 91.32) * mm, "end": v(-113, 88.32) * mm});
            skLineSegment(sketch, "E49.4.0.2", {"start": v(-118, 88.32) * mm, "end": v(-118, 91.32) * mm});
            skLineSegment(sketch, "E49.4.0.3", {"start": v(-118, 91.32) * mm, "end": v(-113, 91.32) * mm});
            skLineSegment(sketch, "E49.5.0.0", {"start": v(-113, 88.32) * mm, "end": v(-108, 88.32) * mm});
            skLineSegment(sketch, "E49.5.0.1", {"start": v(-103, 91.32) * mm, "end": v(-103, 88.32) * mm});
            skLineSegment(sketch, "E49.5.0.2", {"start": v(-108, 88.32) * mm, "end": v(-108, 91.32) * mm});
            skLineSegment(sketch, "E49.5.0.3", {"start": v(-108, 91.32) * mm, "end": v(-103, 91.32) * mm});
            skLineSegment(sketch, "E49.6.0.0", {"start": v(-103, 88.32) * mm, "end": v(-98, 88.32) * mm});
            skLineSegment(sketch, "E49.6.0.1", {"start": v(-93, 91.32) * mm, "end": v(-93, 88.32) * mm});
            skLineSegment(sketch, "E49.6.0.2", {"start": v(-98, 88.32) * mm, "end": v(-98, 91.32) * mm});
            skLineSegment(sketch, "E49.6.0.3", {"start": v(-98, 91.32) * mm, "end": v(-93, 91.32) * mm});
            skLineSegment(sketch, "E49.7.0.0", {"start": v(-93, 88.32) * mm, "end": v(-88, 88.32) * mm});
            skLineSegment(sketch, "E49.7.0.1", {"start": v(-83, 91.32) * mm, "end": v(-83, 88.32) * mm});
            skLineSegment(sketch, "E49.7.0.2", {"start": v(-88, 88.32) * mm, "end": v(-88, 91.32) * mm});
            skLineSegment(sketch, "E49.7.0.3", {"start": v(-88, 91.32) * mm, "end": v(-83, 91.32) * mm});
            skLineSegment(sketch, "E49.8.0.0", {"start": v(-83, 88.32) * mm, "end": v(-78, 88.32) * mm});
            skLineSegment(sketch, "E49.8.0.1", {"start": v(-73, 91.32) * mm, "end": v(-73, 88.32) * mm});
            skLineSegment(sketch, "E49.8.0.2", {"start": v(-78, 88.32) * mm, "end": v(-78, 91.32) * mm});
            skLineSegment(sketch, "E49.8.0.3", {"start": v(-78, 91.32) * mm, "end": v(-73, 91.32) * mm});
            skLineSegment(sketch, "E50", {"start": v(-73, 88.32) * mm, "end": v(-71, 88.32) * mm});
            skLineSegment(sketch, "E51", {"start": v(-71, 88.32) * mm, "end": v(-71, 83.32) * mm});
            skLineSegment(sketch, "E52", {"start": v(-71, 83.32) * mm, "end": v(-68, 83.32) * mm});
            skLineSegment(sketch, "E53", {"start": v(-68, 83.32) * mm, "end": v(-68, 78.32) * mm});
            skLineSegment(sketch, "E54", {"start": v(-68, 78.32) * mm, "end": v(-71, 78.32) * mm});
            skLineSegment(sketch, "E55.0.1.0", {"start": v(-68, 68.32) * mm, "end": v(-71, 68.32) * mm});
            skLineSegment(sketch, "E55.0.1.1", {"start": v(-71, 73.32) * mm, "end": v(-68, 73.32) * mm});
            skLineSegment(sketch, "E55.0.1.2", {"start": v(-68, 73.32) * mm, "end": v(-68, 68.32) * mm});
            skLineSegment(sketch, "E55.0.1.3", {"start": v(-71, 78.32) * mm, "end": v(-71, 73.32) * mm});
            skLineSegment(sketch, "E55.0.2.0", {"start": v(-68, 58.32) * mm, "end": v(-71, 58.32) * mm});
            skLineSegment(sketch, "E55.0.2.1", {"start": v(-71, 63.32) * mm, "end": v(-68, 63.32) * mm});
            skLineSegment(sketch, "E55.0.2.2", {"start": v(-68, 63.32) * mm, "end": v(-68, 58.32) * mm});
            skLineSegment(sketch, "E55.0.2.3", {"start": v(-71, 68.32) * mm, "end": v(-71, 63.32) * mm});
            skLineSegment(sketch, "E55.0.3.0", {"start": v(-68, 48.32) * mm, "end": v(-71, 48.32) * mm});
            skLineSegment(sketch, "E55.0.3.1", {"start": v(-71, 53.32) * mm, "end": v(-68, 53.32) * mm});
            skLineSegment(sketch, "E55.0.3.2", {"start": v(-68, 53.32) * mm, "end": v(-68, 48.32) * mm});
            skLineSegment(sketch, "E55.0.3.3", {"start": v(-71, 58.32) * mm, "end": v(-71, 53.32) * mm});
            skLineSegment(sketch, "E55.0.4.0", {"start": v(-68, 38.32) * mm, "end": v(-71, 38.32) * mm});
            skLineSegment(sketch, "E55.0.4.1", {"start": v(-71, 43.32) * mm, "end": v(-68, 43.32) * mm});
            skLineSegment(sketch, "E55.0.4.2", {"start": v(-68, 43.32) * mm, "end": v(-68, 38.32) * mm});
            skLineSegment(sketch, "E55.0.4.3", {"start": v(-71, 48.32) * mm, "end": v(-71, 43.32) * mm});
            skLineSegment(sketch, "E55.0.5.1", {"start": v(-71, 33.32) * mm, "end": v(-68, 33.32) * mm});
            skLineSegment(sketch, "E55.0.5.2", {"start": v(-68, 33.32) * mm, "end": v(-68, 28.32) * mm});
            skLineSegment(sketch, "E55.0.5.3", {"start": v(-71, 38.32) * mm, "end": v(-71, 33.32) * mm});
            skLineSegment(sketch, "E55.direction1", {"start": v(-71, 78.32) * mm, "end": v(-46, 78.32) * mm, "construction": true});
            skLineSegment(sketch, "E55.direction2", {"start": v(-71, 78.32) * mm, "end": v(-71, 68.32) * mm, "construction": true});
            skLineSegment(sketch, "E56", {"start": v(-68, 28.32) * mm, "end": v(-163, 28.32) * mm});
            skLineSegment(sketch, "E57", {"start": v(-163, 28.32) * mm, "end": v(-163, 33.32) * mm});
            skLineSegment(sketch, "E58", {"start": v(-163, 33.32) * mm, "end": v(-160, 33.32) * mm});
            skLineSegment(sketch, "E59", {"start": v(-160, 33.32) * mm, "end": v(-160, 38.32) * mm});
            skLineSegment(sketch, "E60", {"start": v(-160, 38.32) * mm, "end": v(-163, 38.32) * mm});
            skLineSegment(sketch, "E61.0.1.0", {"start": v(-160, 48.32) * mm, "end": v(-163, 48.32) * mm});
            skLineSegment(sketch, "E61.0.1.1", {"start": v(-163, 43.32) * mm, "end": v(-160, 43.32) * mm});
            skLineSegment(sketch, "E61.0.1.2", {"start": v(-160, 43.32) * mm, "end": v(-160, 48.32) * mm});
            skLineSegment(sketch, "E61.0.1.3", {"start": v(-163, 38.32) * mm, "end": v(-163, 43.32) * mm});
            skLineSegment(sketch, "E61.0.2.0", {"start": v(-160, 58.32) * mm, "end": v(-163, 58.32) * mm});
            skLineSegment(sketch, "E61.0.2.1", {"start": v(-163, 53.32) * mm, "end": v(-160, 53.32) * mm});
            skLineSegment(sketch, "E61.0.2.2", {"start": v(-160, 53.32) * mm, "end": v(-160, 58.32) * mm});
            skLineSegment(sketch, "E61.0.2.3", {"start": v(-163, 48.32) * mm, "end": v(-163, 53.32) * mm});
            skLineSegment(sketch, "E61.0.3.0", {"start": v(-160, 68.32) * mm, "end": v(-163, 68.32) * mm});
            skLineSegment(sketch, "E61.0.3.1", {"start": v(-163, 63.32) * mm, "end": v(-160, 63.32) * mm});
            skLineSegment(sketch, "E61.0.3.2", {"start": v(-160, 63.32) * mm, "end": v(-160, 68.32) * mm});
            skLineSegment(sketch, "E61.0.3.3", {"start": v(-163, 58.32) * mm, "end": v(-163, 63.32) * mm});
            skLineSegment(sketch, "E61.0.4.0", {"start": v(-160, 78.32) * mm, "end": v(-163, 78.32) * mm});
            skLineSegment(sketch, "E61.0.4.1", {"start": v(-163, 73.32) * mm, "end": v(-160, 73.32) * mm});
            skLineSegment(sketch, "E61.0.4.2", {"start": v(-160, 73.32) * mm, "end": v(-160, 78.32) * mm});
            skLineSegment(sketch, "E61.0.4.3", {"start": v(-163, 68.32) * mm, "end": v(-163, 73.32) * mm});
            skLineSegment(sketch, "E61.0.5.1", {"start": v(-163, 83.32) * mm, "end": v(-160, 83.32) * mm});
            skLineSegment(sketch, "E61.0.5.2", {"start": v(-160, 83.32) * mm, "end": v(-160, 88.32) * mm});
            skLineSegment(sketch, "E61.0.5.3", {"start": v(-163, 78.32) * mm, "end": v(-163, 83.32) * mm});
            skLineSegment(sketch, "E61.direction1", {"start": v(-163, 28.32) * mm, "end": v(-138, 28.32) * mm, "construction": true});
            skLineSegment(sketch, "E61.direction2", {"start": v(-163, 28.32) * mm, "end": v(-163, 38.32) * mm, "construction": true});
            skLineSegment(sketch, "E62", {"start": v(-160, 88.32) * mm, "end": v(-158, 88.32) * mm});
            skSolve(sketch);
        }
        {
            var Q0;
            Q0 = qSketchRegion(id + "F8", true);
            extrude(context, id + "F9", {"entities" : qUnion([Q0]), "depth" : 3 * mm});
        }
    });
